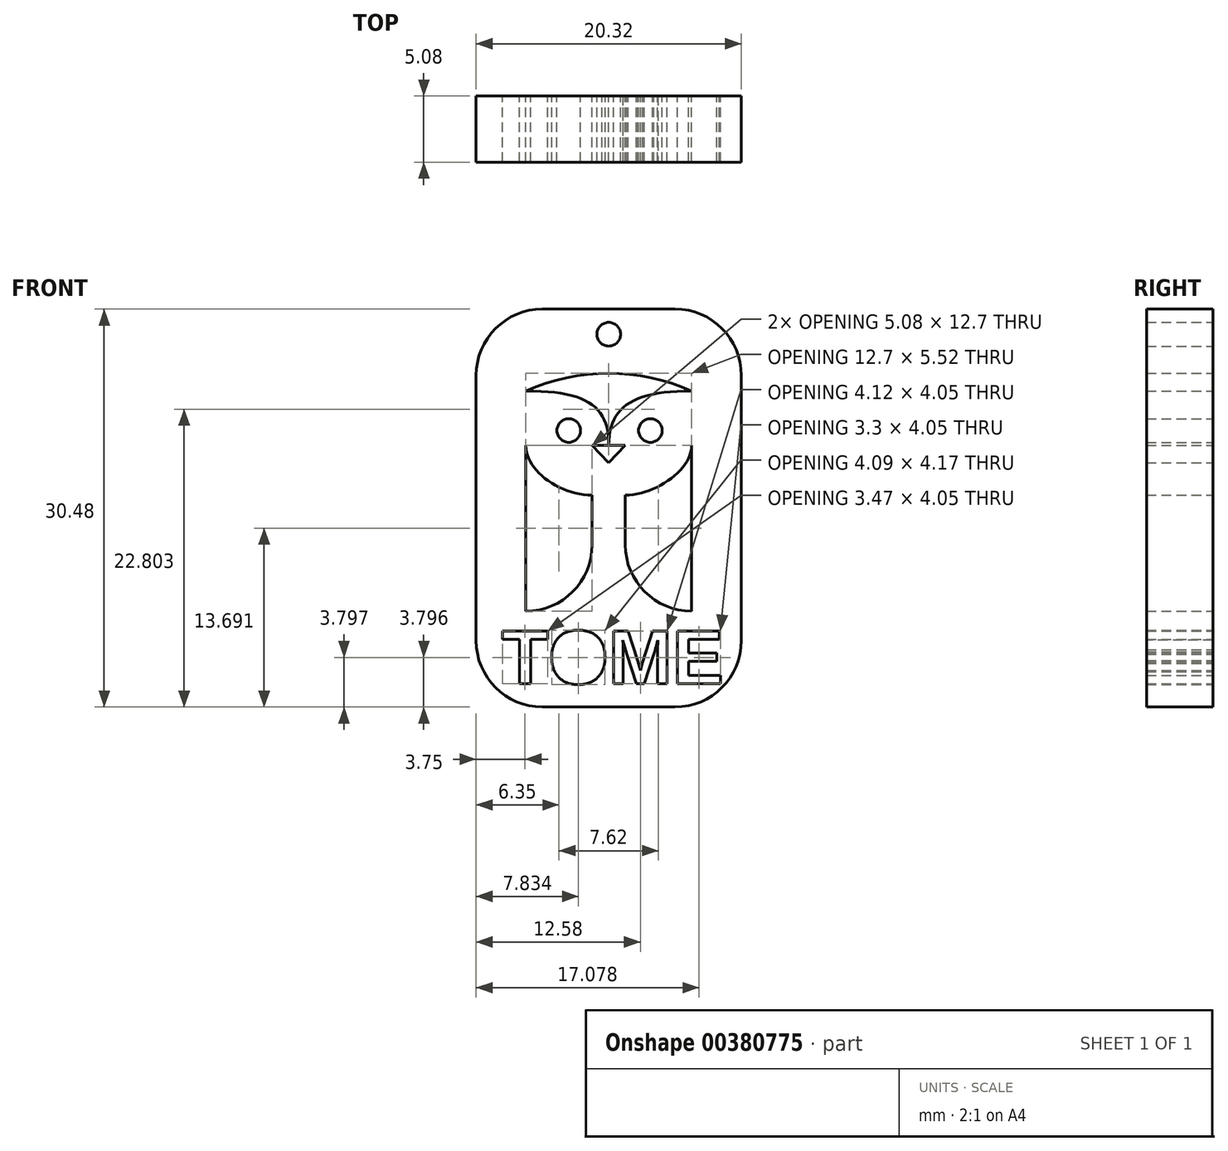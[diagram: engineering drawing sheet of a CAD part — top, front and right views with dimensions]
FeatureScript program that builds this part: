
annotation { "Feature Type Name" : "Feature", "Feature Type Description" : "" }
export const myFeature = defineFeature(function(context is Context, id is Id, definition is map)
    precondition{}
    {
        {
            var Q0;
            Q0=qCreatedBy(makeId("Front.planeOp"),FACE);
            var sketch = newSketch(context, id + "F0", { "sketchPlane" : qUnion([Q0])});
            skLineSegment(sketch, "E0.bottom", {"start": v(10.16, 15.24) * mm, "end": v(-10.16, 15.24) * mm});
            skLineSegment(sketch, "E0.top", {"start": v(10.16, -15.24) * mm, "end": v(-10.16, -15.24) * mm});
            skLineSegment(sketch, "E0.left", {"start": v(10.16, 15.24) * mm, "end": v(10.16, -15.24) * mm});
            skLineSegment(sketch, "E0.right", {"start": v(-10.16, 15.24) * mm, "end": v(-10.16, -15.24) * mm});
            skPoint(sketch, "E0.middle", {"position": v(0, 0) * mm});
            skLineSegment(sketch, "E1.bottom", {"start": v(-6.35, 1) * mm, "end": v(-1.27, 1) * mm});
            skLineSegment(sketch, "E1.top", {"start": v(-6.35, -2.82) * mm, "end": v(-1.27, -2.82) * mm});
            skLineSegment(sketch, "E1.left", {"start": v(-6.35, 1) * mm, "end": v(-6.35, -2.82) * mm});
            skLineSegment(sketch, "E1.right", {"start": v(-1.27, 1) * mm, "end": v(-1.27, -2.82) * mm});
            skLineSegment(sketch, "E2.bottom", {"start": v(1.27, 1) * mm, "end": v(6.35, 1) * mm});
            skLineSegment(sketch, "E2.top", {"start": v(1.27, -2.82) * mm, "end": v(6.35, -2.82) * mm});
            skLineSegment(sketch, "E2.left", {"start": v(1.27, 1) * mm, "end": v(1.27, -2.82) * mm});
            skLineSegment(sketch, "E2.right", {"start": v(6.35, 1) * mm, "end": v(6.35, -2.82) * mm});
            skLineSegment(sketch, "E3", {"start": v(-6.35, -2.82) * mm, "end": v(-6.35, -7.9) * mm});
            skLineSegment(sketch, "E4", {"start": v(6.35, -2.82) * mm, "end": v(6.35, -7.9) * mm});
            skArc(sketch, "E5", {"start": v(-1.27, -2.82) * mm, "mid": v(-2.76, -6.41) * mm, "end": v(-6.35, -7.9) * mm});
            skArc(sketch, "E6", {"start": v(1.27, -2.82) * mm, "mid": v(2.76, -6.41) * mm, "end": v(6.35, -7.9) * mm});
            skLineSegment(sketch, "E7", {"start": v(6.35, 1) * mm, "end": v(6.35, 4.8) * mm});
            skLineSegment(sketch, "E8", {"start": v(-6.35, 1) * mm, "end": v(-6.35, 4.8) * mm});
            skFitSpline(sketch, "E9", {"points": [v(-1.27, 1) * mm, v(-6.35, 4.8) * mm], "startDerivative": vector(-7.62, 0) * mm, "endDerivative": vector(0, 5.71) * mm});
            skFitSpline(sketch, "E10", {"points": [v(1.27, 1) * mm, v(6.35, 4.8) * mm], "startDerivative": vector(6.78, 0) * mm, "endDerivative": vector(0, 5.71) * mm});
            skPoint(sketch, "E11", {"position": v(0, 4.8) * mm});
            skLineSegment(sketch, "E12", {"start": v(0, 4.8) * mm, "end": v(1.27, 4.8) * mm});
            skLineSegment(sketch, "E13", {"start": v(0, 4.8) * mm, "end": v(-1.27, 4.8) * mm});
            skLineSegment(sketch, "E14", {"start": v(-1.27, 4.8) * mm, "end": v(0, 3.47) * mm});
            skLineSegment(sketch, "E15", {"start": v(0, 3.47) * mm, "end": v(1.27, 4.8) * mm});
            skCircle(sketch, "E16", {"center": v(-3.06, 5.94) * mm, "radius": 0.9 * mm});
            skCircle(sketch, "E17", {"center": v(3.2, 5.94) * mm, "radius": 0.9 * mm});
            skPoint(sketch, "E18", {"position": v(6.35, 8.97) * mm});
            skPoint(sketch, "E19", {"position": v(-6.35, 8.97) * mm});
            skFitSpline(sketch, "E20", {"points": [v(0, 4.8) * mm, v(6.35, 8.97) * mm], "startDerivative": vector(0, 8.84) * mm, "endDerivative": vector(13.48, 0) * mm});
            skFitSpline(sketch, "E21", {"points": [v(0, 4.8) * mm, v(-6.35, 8.97) * mm], "startDerivative": vector(0, 8.84) * mm, "endDerivative": vector(-14.27, 0) * mm});
            skArc(sketch, "E22", {"start": v(6.35, 8.97) * mm, "mid": v(0, 10.32) * mm, "end": v(-6.35, 8.97) * mm});
            skText(sketch, "E23", { "text": "TOME", "fontName": "Arimo-Bold.ttf"});
            skCircle(sketch, "E24", {"center": v(0, 13.3) * mm, "radius": 0.9 * mm});
            const initialGuessF0  = {"E23": [-0.00821, -0.01347, 1, 0, 0.00424]};
            skSetInitialGuess(sketch, initialGuessF0);
            skSolve(sketch);
        }
        {
            var Q0;
            Q0 = qSketchRegion(id + "F0", true);
            extrude(context, id + "F1", {"entities" : qUnion([Q0]), "depth" : 5.08 * mm});
        }
        {
            var Q0;
            Q0=makeQuery(id+"F1.opExtrude","SWEPT_EDGE",EDGE,{"disambiguationData":[OSD([sQuery(id+"F0.wireOp",EDGE,"E0.bottom"),sQuery(id+"F0.wireOp",EDGE,"E0.right")])]});
            var Q1;
            Q1=makeQuery(id+"F1.opExtrude","SWEPT_EDGE",EDGE,{"disambiguationData":[OSD([sQuery(id+"F0.wireOp",EDGE,"E0.bottom"),sQuery(id+"F0.wireOp",EDGE,"E0.left")])]});
            var Q2;
            Q2=makeQuery(id+"F1.opExtrude","SWEPT_EDGE",EDGE,{"disambiguationData":[OSD([sQuery(id+"F0.wireOp",EDGE,"E0.top"),sQuery(id+"F0.wireOp",EDGE,"E0.left")])]});
            var Q3;
            Q3=makeQuery(id+"F1.opExtrude","SWEPT_EDGE",EDGE,{"disambiguationData":[OSD([sQuery(id+"F0.wireOp",EDGE,"E0.top"),sQuery(id+"F0.wireOp",EDGE,"E0.right")])]});
            fillet(context, id + "F2", {"entities" : qUnion([Q0, Q1, Q2, Q3]), "radius" : 5.08 * mm, "tangentPropagation" : true, "allowEdgeOverflow" : false});
        }
    });
